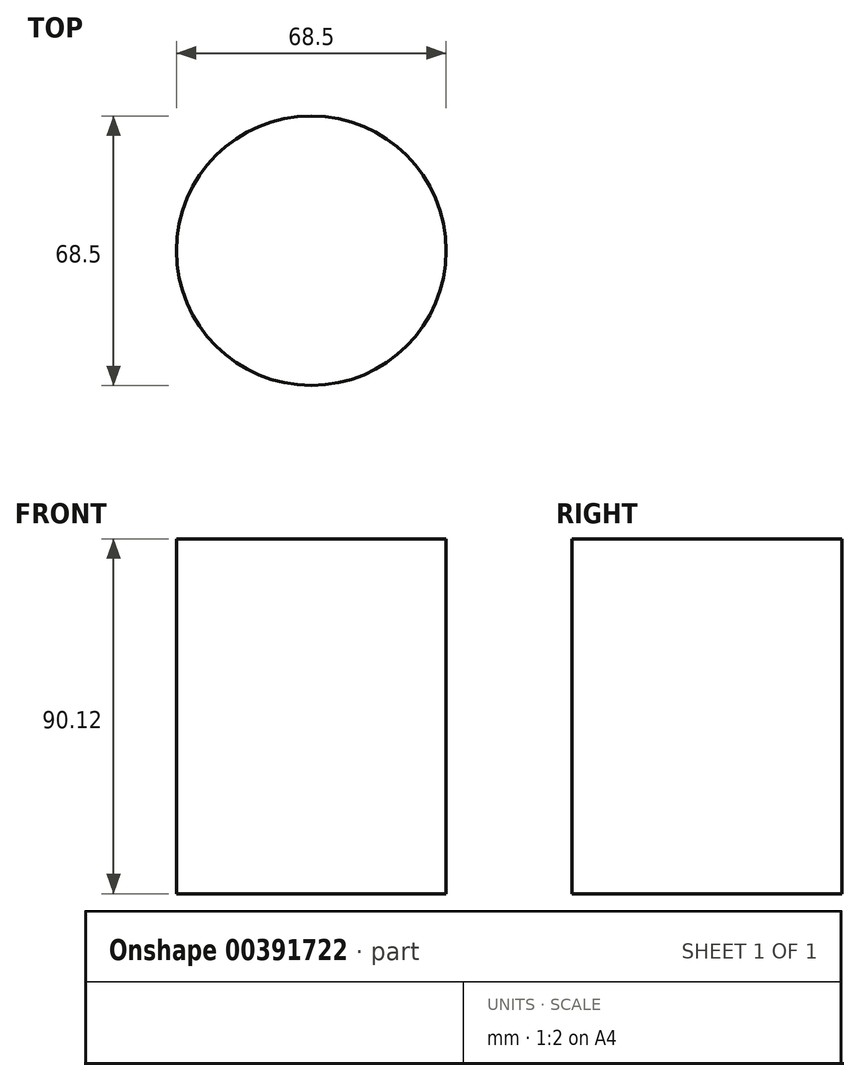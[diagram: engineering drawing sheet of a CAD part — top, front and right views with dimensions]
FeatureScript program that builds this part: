
annotation { "Feature Type Name" : "Feature", "Feature Type Description" : "" }
export const myFeature = defineFeature(function(context is Context, id is Id, definition is map)
    precondition{}
    {
        {
            var Q0;
            Q0=qCreatedBy(makeId("Front.planeOp"),FACE);
            var sketch = newSketch(context, id + "F0", { "sketchPlane" : qUnion([Q0])});
            skLineSegment(sketch, "E0", {"start": v(0, 55.3) * mm, "end": v(34.25, 55.3) * mm});
            skLineSegment(sketch, "E1", {"start": v(34.25, 55.3) * mm, "end": v(34.25, -34.81) * mm});
            skLineSegment(sketch, "E2", {"start": v(34.25, -34.81) * mm, "end": v(0, -34.81) * mm});
            skLineSegment(sketch, "E3", {"start": v(0, -34.81) * mm, "end": v(0, 55.3) * mm});
            skSolve(sketch);
        }
        {
            var Q0;
            Q0=makeQuery(id+"F0.imprint","IMPRINT",FACE,{"disambiguationData":[TD([[makeQuery(id+"F0.imprint","IMPRINT",EDGE,{"derivedFrom":sQuery(id+"F0.wireOp",EDGE,"E0")}),-1.0]])]});
            var Q1;
            Q1=sQuery(id+"F0.wireOp",EDGE,"E3");
            revolve(context, id + "F1", {"entities" : qUnion([Q0]), "axis" : qUnion([Q1]), "revolveType" : RevolveType.FULL});
        }
    });
